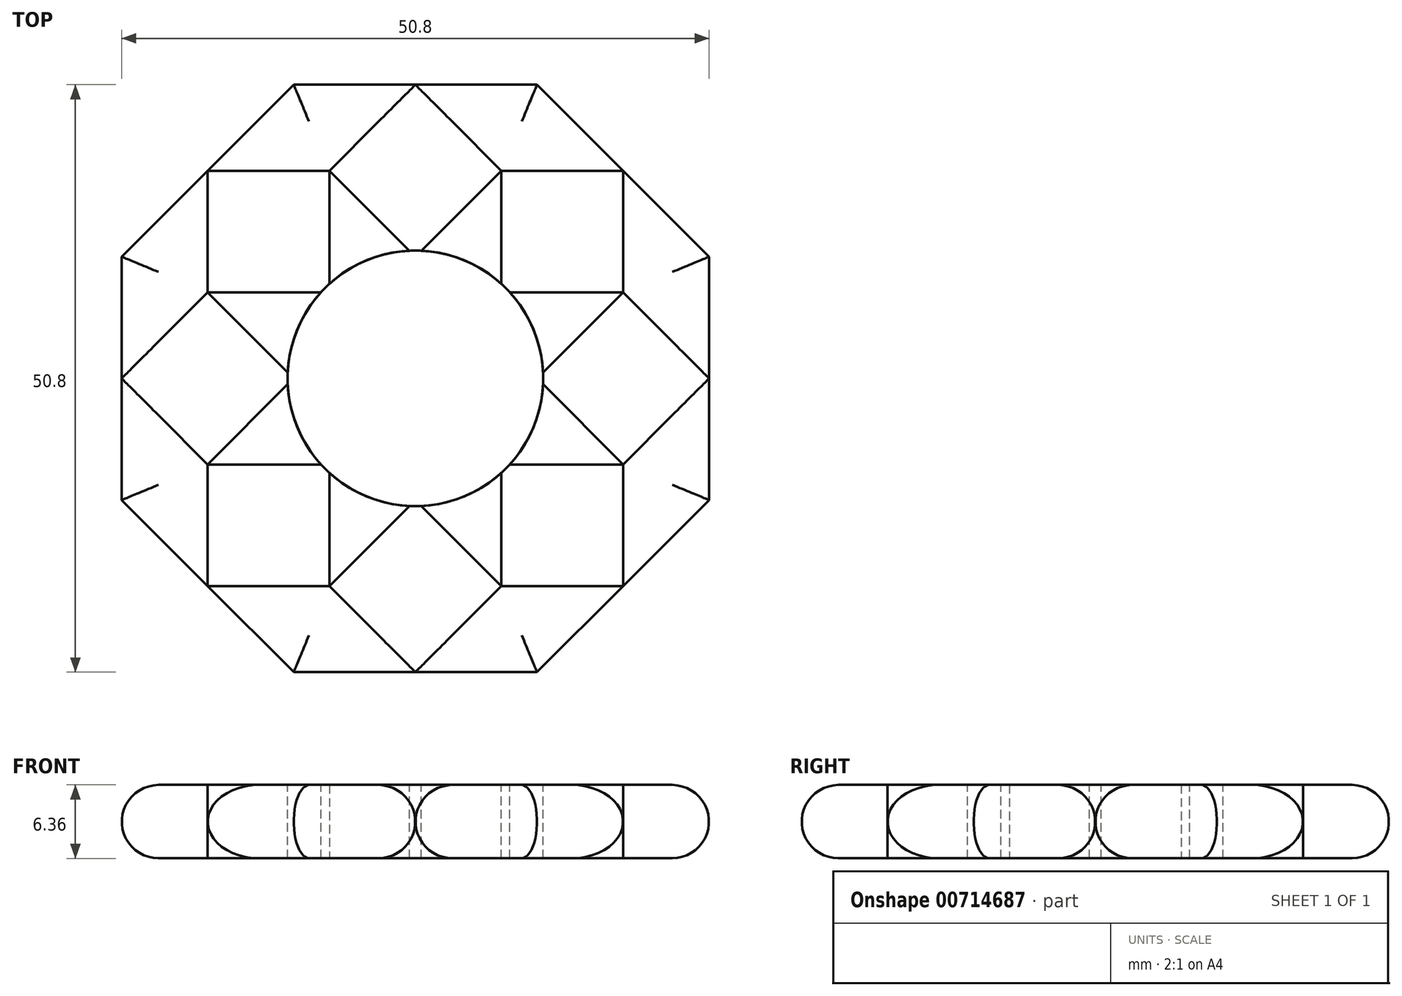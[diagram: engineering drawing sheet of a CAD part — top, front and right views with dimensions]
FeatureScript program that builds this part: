
annotation { "Feature Type Name" : "Feature", "Feature Type Description" : "" }
export const myFeature = defineFeature(function(context is Context, id is Id, definition is map)
    precondition{}
    {
        {
            var Q0;
            Q0=qCreatedBy(makeId("Top.planeOp"),FACE);
            var sketch = newSketch(context, id + "F0", { "sketchPlane" : qUnion([Q0])});
            skCircle(sketch, "E0.cCircle", {"center": v(0, -12.7) * mm, "radius": 12.7 * mm, "construction": true});
            skLineSegment(sketch, "E0.0", {"start": v(-5.26, 0) * mm, "end": v(5.26, 0) * mm});
            skLineSegment(sketch, "E0.1", {"start": v(5.26, 0) * mm, "end": v(12.7, -7.44) * mm});
            skLineSegment(sketch, "E0.2", {"start": v(12.7, -7.44) * mm, "end": v(12.7, -17.96) * mm});
            skLineSegment(sketch, "E0.3", {"start": v(12.7, -17.96) * mm, "end": v(5.26, -25.4) * mm});
            skLineSegment(sketch, "E0.4", {"start": v(5.26, -25.4) * mm, "end": v(-5.26, -25.4) * mm});
            skLineSegment(sketch, "E0.5", {"start": v(-5.26, -25.4) * mm, "end": v(-12.7, -17.96) * mm});
            skLineSegment(sketch, "E0.6", {"start": v(-12.7, -17.96) * mm, "end": v(-12.7, -7.44) * mm});
            skLineSegment(sketch, "E0.7", {"start": v(-12.7, -7.44) * mm, "end": v(-5.26, 0) * mm});
            skPoint(sketch, "E0.0.midPoint", {"position": v(0, 0) * mm});
            skSolve(sketch);
        }
        {
            var Q0;
            Q0=makeQuery(id+"F0.imprint","IMPRINT",FACE,{"disambiguationData":[TD([[makeQuery(id+"F0.imprint","IMPRINT",EDGE,{"derivedFrom":sQuery(id+"F0.wireOp",EDGE,"E0.0")}),-1.0]])]});
            extrude(context, id + "F1", {"entities" : qUnion([Q0]), "endBound" : BoundingType.SYMMETRIC, "depth" : 6.35 * mm, "offsetDistance" : 25.4 * mm});
        }
        {
            var Q0;
            Q0=makeQuery(id+"F1.opExtrude","SWEPT_BODY",BODY,{"disambiguationData":[OSD([sQuery(id+"F0.wireOp",EDGE,"E0.0"),sQuery(id+"F0.wireOp",EDGE,"E0.1"),sQuery(id+"F0.wireOp",EDGE,"E0.2"),sQuery(id+"F0.wireOp",EDGE,"E0.3"),sQuery(id+"F0.wireOp",EDGE,"E0.4"),sQuery(id+"F0.wireOp",EDGE,"E0.5"),sQuery(id+"F0.wireOp",EDGE,"E0.6"),sQuery(id+"F0.wireOp",EDGE,"E0.7")])]});
            var Q1;
            Q1=makeQuery(id+"F1.opExtrude","SWEPT_EDGE",EDGE,{"disambiguationData":[OSD([sQuery(id+"F0.wireOp",EDGE,"E0.0"),sQuery(id+"F0.wireOp",EDGE,"E0.1")])]});
            circularPattern(context, id + "F2", {"entities" : qUnion([Q0]), "axis" : qUnion([Q1]), "angle" : 360 * degree, "instanceCount" : 8, "oppositeDirection" : true, "equalSpace" : true});
        }
        {
            var Q0;
            Q0=qCreatedBy(makeId("Top.planeOp"),FACE);
            var sketch = newSketch(context, id + "F3", { "sketchPlane" : qUnion([Q0])});
            skCircle(sketch, "E1", {"center": v(5.26, 0) * mm, "radius": 11.05 * mm});
            skSolve(sketch);
        }
        {
            var Q0;
            Q0 = qSketchRegion(id + "F3", true);
            extrude(context, id + "F4", {"entities" : qUnion([Q0]), "operationType" : NewBodyOperationType.REMOVE, "endBound" : BoundingType.SYMMETRIC, "oppositeDirection" : true, "depth" : 25.4 * mm, "offsetDistance" : 25.4 * mm});
        }
        {
            var Q0;
            Q0=makeQuery(id+"F2.opPattern","COPY",EDGE,{"derivedFrom":makeQuery(id+"F1.opExtrude","CAP_EDGE",EDGE,{"disambiguationData":[OSD([sQuery(id+"F0.wireOp",EDGE,"E0.4")])],"isStart":false}),"instanceName":"2"});
            var Q1;
            Q1=makeQuery(id+"F2.opPattern","COPY",EDGE,{"derivedFrom":makeQuery(id+"F1.opExtrude","CAP_EDGE",EDGE,{"disambiguationData":[OSD([sQuery(id+"F0.wireOp",EDGE,"E0.5")])],"isStart":false}),"instanceName":"3"});
            var Q2;
            Q2=makeQuery(id+"F2.opPattern","COPY",EDGE,{"derivedFrom":makeQuery(id+"F1.opExtrude","CAP_EDGE",EDGE,{"disambiguationData":[OSD([sQuery(id+"F0.wireOp",EDGE,"E0.4")])],"isStart":false}),"instanceName":"3"});
            var Q3;
            Q3=makeQuery(id+"F2.opPattern","COPY",EDGE,{"derivedFrom":makeQuery(id+"F1.opExtrude","CAP_EDGE",EDGE,{"disambiguationData":[OSD([sQuery(id+"F0.wireOp",EDGE,"E0.5")])],"isStart":false}),"instanceName":"4"});
            var Q4;
            Q4=makeQuery(id+"F2.opPattern","COPY",EDGE,{"derivedFrom":makeQuery(id+"F1.opExtrude","CAP_EDGE",EDGE,{"disambiguationData":[OSD([sQuery(id+"F0.wireOp",EDGE,"E0.4")])],"isStart":false}),"instanceName":"4"});
            var Q5;
            Q5=makeQuery(id+"F2.opPattern","COPY",EDGE,{"derivedFrom":makeQuery(id+"F1.opExtrude","CAP_EDGE",EDGE,{"disambiguationData":[OSD([sQuery(id+"F0.wireOp",EDGE,"E0.5")])],"isStart":false}),"instanceName":"5"});
            var Q6;
            Q6=makeQuery(id+"F2.opPattern","COPY",EDGE,{"derivedFrom":makeQuery(id+"F1.opExtrude","CAP_EDGE",EDGE,{"disambiguationData":[OSD([sQuery(id+"F0.wireOp",EDGE,"E0.5")])],"isStart":false}),"instanceName":"6"});
            var Q7;
            Q7=makeQuery(id+"F2.opPattern","COPY",EDGE,{"derivedFrom":makeQuery(id+"F1.opExtrude","CAP_EDGE",EDGE,{"disambiguationData":[OSD([sQuery(id+"F0.wireOp",EDGE,"E0.4")])],"isStart":false}),"instanceName":"5"});
            var Q8;
            Q8=makeQuery(id+"F2.opPattern","COPY",EDGE,{"derivedFrom":makeQuery(id+"F1.opExtrude","CAP_EDGE",EDGE,{"disambiguationData":[OSD([sQuery(id+"F0.wireOp",EDGE,"E0.5")])],"isStart":false}),"instanceName":"7"});
            var Q9;
            Q9=makeQuery(id+"F2.opPattern","COPY",EDGE,{"derivedFrom":makeQuery(id+"F1.opExtrude","CAP_EDGE",EDGE,{"disambiguationData":[OSD([sQuery(id+"F0.wireOp",EDGE,"E0.4")])],"isStart":false}),"instanceName":"6"});
            var Q10;
            Q10=makeQuery(id+"F2.opPattern","COPY",EDGE,{"derivedFrom":makeQuery(id+"F1.opExtrude","CAP_EDGE",EDGE,{"disambiguationData":[OSD([sQuery(id+"F0.wireOp",EDGE,"E0.4")])],"isStart":false}),"instanceName":"7"});
            var Q11;
            Q11=makeQuery(id+"F1.opExtrude","CAP_EDGE",EDGE,{"disambiguationData":[OSD([sQuery(id+"F0.wireOp",EDGE,"E0.5")])],"isStart":false});
            var Q12;
            Q12=makeQuery(id+"F1.opExtrude","CAP_EDGE",EDGE,{"disambiguationData":[OSD([sQuery(id+"F0.wireOp",EDGE,"E0.4")])],"isStart":false});
            var Q13;
            Q13=makeQuery(id+"F2.opPattern","COPY",EDGE,{"derivedFrom":makeQuery(id+"F1.opExtrude","CAP_EDGE",EDGE,{"disambiguationData":[OSD([sQuery(id+"F0.wireOp",EDGE,"E0.5")])],"isStart":false}),"instanceName":"1"});
            var Q14;
            Q14=makeQuery(id+"F2.opPattern","COPY",EDGE,{"derivedFrom":makeQuery(id+"F1.opExtrude","CAP_EDGE",EDGE,{"disambiguationData":[OSD([sQuery(id+"F0.wireOp",EDGE,"E0.4")])],"isStart":false}),"instanceName":"1"});
            var Q15;
            Q15=makeQuery(id+"F2.opPattern","COPY",EDGE,{"derivedFrom":makeQuery(id+"F1.opExtrude","CAP_EDGE",EDGE,{"disambiguationData":[OSD([sQuery(id+"F0.wireOp",EDGE,"E0.5")])],"isStart":false}),"instanceName":"2"});
            var Q16;
            Q16=makeQuery(id+"F2.opPattern","COPY",EDGE,{"derivedFrom":makeQuery(id+"F1.opExtrude","CAP_EDGE",EDGE,{"disambiguationData":[OSD([sQuery(id+"F0.wireOp",EDGE,"E0.5")])],"isStart":true}),"instanceName":"2"});
            var Q17;
            Q17=makeQuery(id+"F2.opPattern","COPY",EDGE,{"derivedFrom":makeQuery(id+"F1.opExtrude","CAP_EDGE",EDGE,{"disambiguationData":[OSD([sQuery(id+"F0.wireOp",EDGE,"E0.4")])],"isStart":true}),"instanceName":"2"});
            var Q18;
            Q18=makeQuery(id+"F2.opPattern","COPY",EDGE,{"derivedFrom":makeQuery(id+"F1.opExtrude","CAP_EDGE",EDGE,{"disambiguationData":[OSD([sQuery(id+"F0.wireOp",EDGE,"E0.5")])],"isStart":true}),"instanceName":"3"});
            var Q19;
            Q19=makeQuery(id+"F2.opPattern","COPY",EDGE,{"derivedFrom":makeQuery(id+"F1.opExtrude","CAP_EDGE",EDGE,{"disambiguationData":[OSD([sQuery(id+"F0.wireOp",EDGE,"E0.5")])],"isStart":true}),"instanceName":"4"});
            var Q20;
            Q20=makeQuery(id+"F2.opPattern","COPY",EDGE,{"derivedFrom":makeQuery(id+"F1.opExtrude","CAP_EDGE",EDGE,{"disambiguationData":[OSD([sQuery(id+"F0.wireOp",EDGE,"E0.4")])],"isStart":true}),"instanceName":"3"});
            var Q21;
            Q21=makeQuery(id+"F2.opPattern","COPY",EDGE,{"derivedFrom":makeQuery(id+"F1.opExtrude","CAP_EDGE",EDGE,{"disambiguationData":[OSD([sQuery(id+"F0.wireOp",EDGE,"E0.4")])],"isStart":true}),"instanceName":"4"});
            var Q22;
            Q22=makeQuery(id+"F2.opPattern","COPY",EDGE,{"derivedFrom":makeQuery(id+"F1.opExtrude","CAP_EDGE",EDGE,{"disambiguationData":[OSD([sQuery(id+"F0.wireOp",EDGE,"E0.5")])],"isStart":true}),"instanceName":"5"});
            var Q23;
            Q23=makeQuery(id+"F2.opPattern","COPY",EDGE,{"derivedFrom":makeQuery(id+"F1.opExtrude","CAP_EDGE",EDGE,{"disambiguationData":[OSD([sQuery(id+"F0.wireOp",EDGE,"E0.4")])],"isStart":true}),"instanceName":"5"});
            var Q24;
            Q24=makeQuery(id+"F2.opPattern","COPY",EDGE,{"derivedFrom":makeQuery(id+"F1.opExtrude","CAP_EDGE",EDGE,{"disambiguationData":[OSD([sQuery(id+"F0.wireOp",EDGE,"E0.5")])],"isStart":true}),"instanceName":"6"});
            var Q25;
            Q25=makeQuery(id+"F2.opPattern","COPY",EDGE,{"derivedFrom":makeQuery(id+"F1.opExtrude","CAP_EDGE",EDGE,{"disambiguationData":[OSD([sQuery(id+"F0.wireOp",EDGE,"E0.4")])],"isStart":true}),"instanceName":"6"});
            var Q26;
            Q26=makeQuery(id+"F2.opPattern","COPY",EDGE,{"derivedFrom":makeQuery(id+"F1.opExtrude","CAP_EDGE",EDGE,{"disambiguationData":[OSD([sQuery(id+"F0.wireOp",EDGE,"E0.5")])],"isStart":true}),"instanceName":"7"});
            var Q27;
            Q27=makeQuery(id+"F2.opPattern","COPY",EDGE,{"derivedFrom":makeQuery(id+"F1.opExtrude","CAP_EDGE",EDGE,{"disambiguationData":[OSD([sQuery(id+"F0.wireOp",EDGE,"E0.4")])],"isStart":true}),"instanceName":"7"});
            var Q28;
            Q28=makeQuery(id+"F1.opExtrude","CAP_EDGE",EDGE,{"disambiguationData":[OSD([sQuery(id+"F0.wireOp",EDGE,"E0.5")])],"isStart":true});
            var Q29;
            Q29=makeQuery(id+"F1.opExtrude","CAP_EDGE",EDGE,{"disambiguationData":[OSD([sQuery(id+"F0.wireOp",EDGE,"E0.4")])],"isStart":true});
            var Q30;
            Q30=makeQuery(id+"F2.opPattern","COPY",EDGE,{"derivedFrom":makeQuery(id+"F1.opExtrude","CAP_EDGE",EDGE,{"disambiguationData":[OSD([sQuery(id+"F0.wireOp",EDGE,"E0.5")])],"isStart":true}),"instanceName":"1"});
            var Q31;
            Q31=makeQuery(id+"F2.opPattern","COPY",EDGE,{"derivedFrom":makeQuery(id+"F1.opExtrude","CAP_EDGE",EDGE,{"disambiguationData":[OSD([sQuery(id+"F0.wireOp",EDGE,"E0.4")])],"isStart":true}),"instanceName":"1"});
            fillet(context, id + "F5", {"entities" : qUnion([Q0, Q1, Q2, Q3, Q4, Q5, Q6, Q7, Q8, Q9, Q10, Q11, Q12, Q13, Q14, Q15, Q16, Q17, Q18, Q19, Q20, Q21, Q22, Q23, Q24, Q25, Q26, Q27, Q28, Q29, Q30, Q31]), "radius" : 3.17 * mm, "tangentPropagation" : true, "allowEdgeOverflow" : false});
        }
    });
